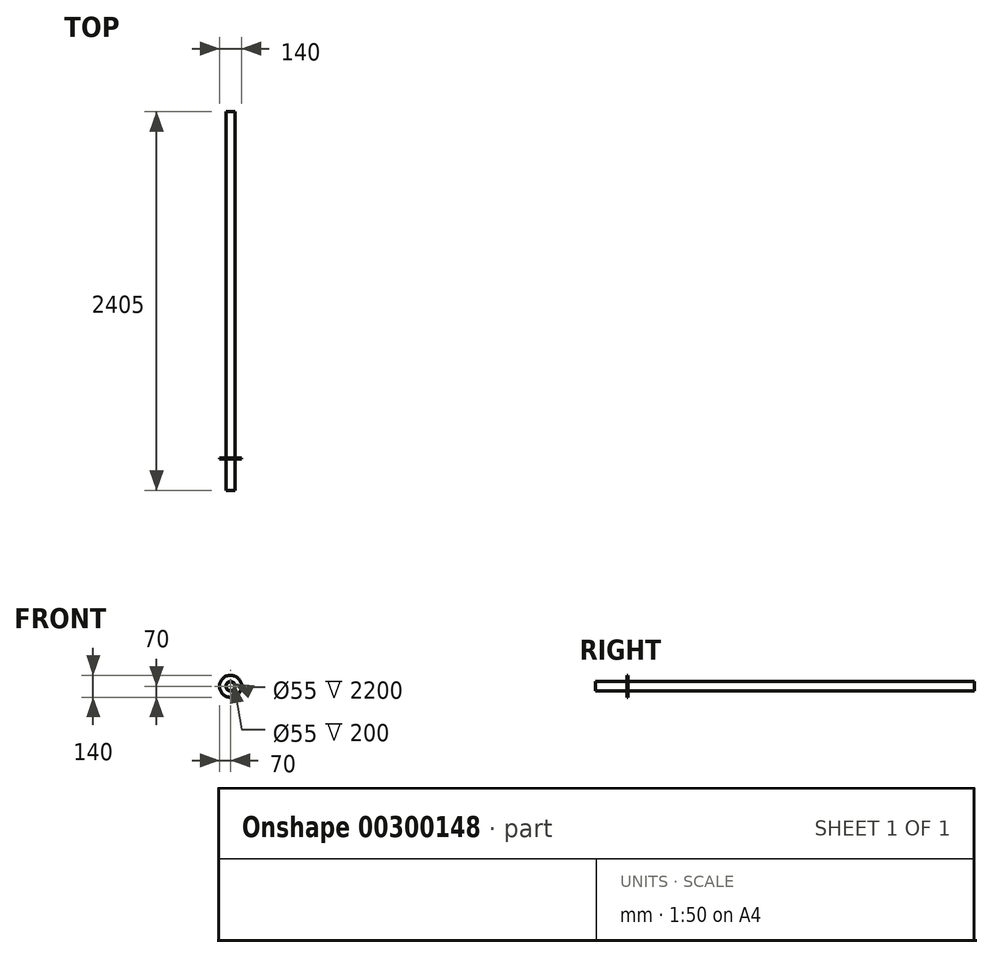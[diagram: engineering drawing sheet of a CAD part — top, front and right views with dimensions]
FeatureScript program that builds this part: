
annotation { "Feature Type Name" : "Feature", "Feature Type Description" : "" }
export const myFeature = defineFeature(function(context is Context, id is Id, definition is map)
    precondition{}
    {
        {
            var Q0;
            Q0=qCreatedBy(makeId("Front.planeOp"),FACE);
            var sketch = newSketch(context, id + "F0", { "sketchPlane" : qUnion([Q0])});
            skCircle(sketch, "E0", {"center": v(0, 0) * mm, "radius": 30 * mm});
            skCircle(sketch, "E1", {"center": v(0, 0) * mm, "radius": 27.5 * mm});
            skSolve(sketch);
        }
        {
            var Q0;
            Q0=makeQuery(id+"F0.imprint","IMPRINT",FACE,{"disambiguationData":[TD([[makeQuery(id+"F0.imprint","IMPRINT",EDGE,{"derivedFrom":sQuery(id+"F0.wireOp",EDGE,"E0")}),1.0]])]});
            extrude(context, id + "F1", {"entities" : qUnion([Q0]), "endBound" : BoundingType.SYMMETRIC, "depth" : 2200 * mm});
        }
        {
            var Q0;
            Q0=makeQuery(id+"F1.opExtrude","CAP_FACE",FACE,{"disambiguationData":[OSD([sQuery(id+"F0.wireOp",EDGE,"E0"),sQuery(id+"F0.wireOp",EDGE,"E1")])],"isStart":false});
            var sketch = newSketch(context, id + "F2", { "sketchPlane" : qUnion([Q0])});
            skCircle(sketch, "E2", {"center": v(0, 0) * mm, "radius": 70 * mm});
            skSolve(sketch);
        }
        {
            var Q0;
            Q0=qSketchRegion(id+"F2",true);
            extrude(context, id + "F3", {"entities" : qUnion([Q0]), "operationType" : NewBodyOperationType.ADD, "depth" : 5 * mm});
        }
        {
            var Q0;
            Q0=makeQuery(id+"F3.opExtrude","CAP_FACE",FACE,{"disambiguationData":[OSD([sQuery(id+"F2.wireOp",EDGE,"E2")])],"isStart":false});
            var sketch = newSketch(context, id + "F4", { "sketchPlane" : qUnion([Q0])});
            skCircle(sketch, "E3", {"center": v(0, 0) * mm, "radius": 30 * mm});
            skCircle(sketch, "E4", {"center": v(0, 0) * mm, "radius": 27.5 * mm});
            skSolve(sketch);
        }
        {
            var Q0;
            Q0=makeQuery(id+"F4.imprint","IMPRINT",FACE,{"disambiguationData":[TD([[makeQuery(id+"F4.imprint","IMPRINT",EDGE,{"derivedFrom":sQuery(id+"F4.wireOp",EDGE,"E3")}),1.0]])]});
            var Q1;
            Q1=sQuery(id+"F4.wireOp",EDGE,"E3");
            var Q2;
            Q2=sQuery(id+"F4.wireOp",EDGE,"E4");
            extrude(context, id + "F5", {"entities" : qUnion([Q0]), "operationType" : NewBodyOperationType.ADD, "surfaceEntities" : qUnion([Q1, Q2]), "depth" : 200 * mm});
        }
    });
